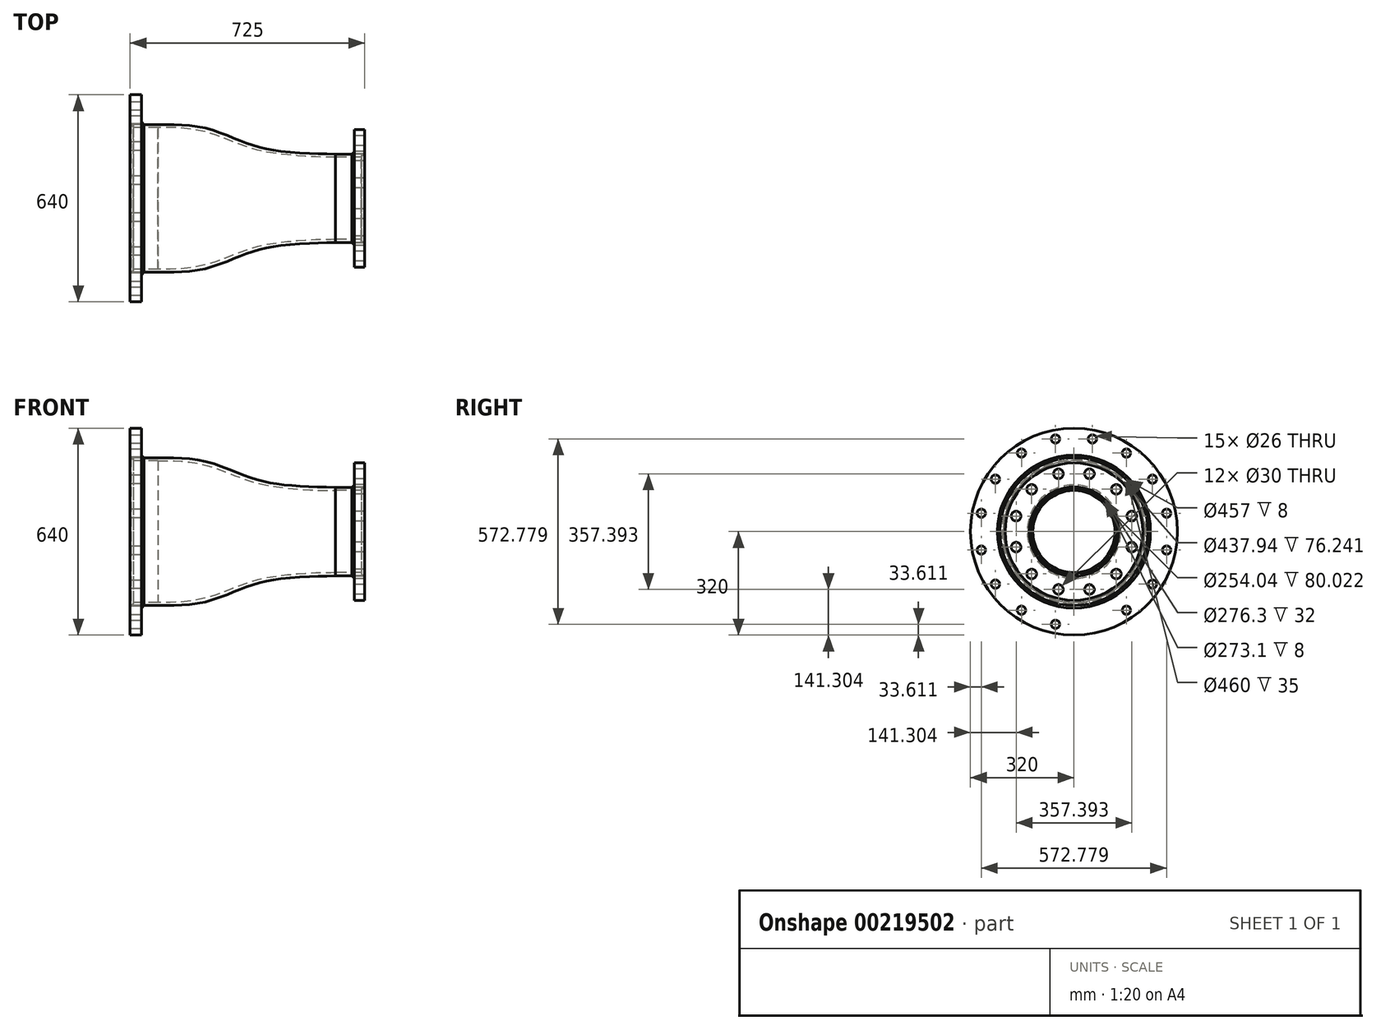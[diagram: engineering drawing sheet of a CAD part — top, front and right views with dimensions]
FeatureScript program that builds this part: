
annotation { "Feature Type Name" : "Feature", "Feature Type Description" : "" }
export const myFeature = defineFeature(function(context is Context, id is Id, definition is map)
    precondition{}
    {
        {
            var Q0;
            Q0=qCreatedBy(makeId("Front.planeOp"),FACE);
            var sketch = newSketch(context, id + "F0", { "sketchPlane" : qUnion([Q0])});
            skLineSegment(sketch, "E0", {"start": v(-562.58, 0) * mm, "end": v(652.64, 0) * mm, "construction": true});
            skLineSegment(sketch, "E1", {"start": v(-329.66, 228.5) * mm, "end": v(-253.37, 228.5) * mm});
            skLineSegment(sketch, "E2", {"start": v(375.34, 136.55) * mm, "end": v(295.32, 136.55) * mm});
            skFitSpline(sketch, "E3", {"points": [v(-253.37, 228.5) * mm, v(-109.72, 217.61) * mm, v(24.3, 169.13) * mm, v(129.85, 145.37) * mm, v(295.32, 136.55) * mm], "startDerivative": vector(539.24, -5.2) * mm, "endDerivative": vector(650.78, -14.67) * mm});
            skLineSegment(sketch, "E4.1", {"start": v(-329.66, 218.97) * mm, "end": v(-253.42, 218.97) * mm});
            skLineSegment(sketch, "E5.0", {"start": v(375.34, 127.02) * mm, "end": v(295.32, 127.02) * mm});
            skLineSegment(sketch, "E6", {"start": v(-329.66, 228.5) * mm, "end": v(-329.66, 218.97) * mm});
            skLineSegment(sketch, "E7", {"start": v(375.34, 136.55) * mm, "end": v(375.34, 127.02) * mm});
            skLineSegment(sketch, "E8.bottom", {"start": v(-304.66, 230) * mm, "end": v(-339.66, 230) * mm});
            skLineSegment(sketch, "E8.top", {"start": v(-304.66, 320) * mm, "end": v(-339.66, 320) * mm});
            skLineSegment(sketch, "E8.left", {"start": v(-304.66, 230) * mm, "end": v(-304.66, 320) * mm});
            skLineSegment(sketch, "E8.right", {"start": v(-339.66, 230) * mm, "end": v(-339.66, 320) * mm});
            skLineSegment(sketch, "E9", {"start": v(-304.66, 230) * mm, "end": v(-304.66, 228.5) * mm});
            skLineSegment(sketch, "E10", {"start": v(-337.66, 230) * mm, "end": v(-329.66, 222) * mm});
            skLineSegment(sketch, "E11", {"start": v(-304.66, 236.5) * mm, "end": v(-296.66, 228.5) * mm});
            skLineSegment(sketch, "E12", {"start": v(-329.66, 230) * mm, "end": v(-329.66, 228.5) * mm});
            skLineSegment(sketch, "E13.bottom", {"start": v(385.34, 138.15) * mm, "end": v(353.34, 138.15) * mm});
            skLineSegment(sketch, "E13.top", {"start": v(385.34, 212.5) * mm, "end": v(353.34, 212.5) * mm});
            skLineSegment(sketch, "E13.left", {"start": v(385.34, 138.15) * mm, "end": v(385.34, 212.5) * mm});
            skLineSegment(sketch, "E13.right", {"start": v(353.34, 138.15) * mm, "end": v(353.34, 212.5) * mm});
            skLineSegment(sketch, "E14", {"start": v(353.34, 138.15) * mm, "end": v(353.34, 136.55) * mm});
            skLineSegment(sketch, "E15", {"start": v(375.34, 138.15) * mm, "end": v(375.34, 136.55) * mm});
            skLineSegment(sketch, "E16", {"start": v(345.34, 136.55) * mm, "end": v(353.34, 144.55) * mm});
            skLineSegment(sketch, "E17", {"start": v(383.34, 138.15) * mm, "end": v(375.34, 130.15) * mm});
            skLineSegment(sketch, "E18", {"start": v(-253.37, 228.5) * mm, "end": v(-253.42, 218.97) * mm});
            skLineSegment(sketch, "E19", {"start": v(295.32, 136.55) * mm, "end": v(295.32, 127.02) * mm});
            skFitSpline(sketch, "E20", {"points": [v(-253.42, 218.97) * mm, v(-209.6, 218.97) * mm, v(-109.6, 206.39) * mm, v(24.68, 158.26) * mm, v(130.86, 136.31) * mm, v(236.57, 128.15) * mm, v(295.32, 127.02) * mm], "startDerivative": vector(341.33, 5.53) * mm, "endDerivative": vector(401.2, -2.2) * mm});
            skSolve(sketch);
        }
        {
            var Q0;
            {var subQ0=sQuery(id+"F0.wireOp",EDGE,"E8.top");Q0=makeQuery(id+"F0.imprint","IMPRINT",FACE,{"disambiguationData":[TD([[makeQuery(id+"F0.imprint","IMPRINT",EDGE,{"derivedFrom":subQ0}),1.0]])]});}
            var Q1;
            Q1=sQuery(id+"F0.wireOp",EDGE,"E0");
            revolve(context, id + "F1", {"entities" : qUnion([Q0]), "axis" : qUnion([Q1]), "revolveType" : RevolveType.FULL});
        }
        {
            var Q0;
            Q0=makeQuery(id+"F0.imprint","IMPRINT",FACE,{"disambiguationData":[TD([[makeQuery(id+"F0.imprint","IMPRINT",EDGE,{"derivedFrom":sQuery(id+"F0.wireOp",EDGE,"E3")}),-1.0]])]});
            var Q1;
            {var subQ0=sQuery(id+"F0.wireOp",EDGE,"E4.1");Q1=makeQuery(id+"F0.imprint","IMPRINT",FACE,{"disambiguationData":[TD([[makeQuery(id+"F0.imprint","IMPRINT",EDGE,{"derivedFrom":subQ0}),1.0]])]});}
            var Q2;
            {var subQ0=sQuery(id+"F0.wireOp",EDGE,"E5.0");Q2=makeQuery(id+"F0.imprint","IMPRINT",FACE,{"disambiguationData":[TD([[makeQuery(id+"F0.imprint","IMPRINT",EDGE,{"derivedFrom":subQ0}),-1.0]])]});}
            var Q3;
            Q3=sQuery(id+"F0.wireOp",EDGE,"E0");
            revolve(context, id + "F2", {"entities" : qUnion([Q0, Q1, Q2]), "axis" : qUnion([Q3]), "revolveType" : RevolveType.FULL});
        }
        {
            var Q0;
            {var subQ0=sQuery(id+"F0.wireOp",EDGE,"E13.top");Q0=makeQuery(id+"F0.imprint","IMPRINT",FACE,{"disambiguationData":[TD([[makeQuery(id+"F0.imprint","IMPRINT",EDGE,{"derivedFrom":subQ0}),1.0]])]});}
            var Q1;
            Q1=sQuery(id+"F0.wireOp",EDGE,"E0");
            revolve(context, id + "F3", {"entities" : qUnion([Q0]), "axis" : qUnion([Q1]), "revolveType" : RevolveType.FULL});
        }
        {
            var Q0;
            {var subQ2=sQuery(id+"F0.wireOp",EDGE,"E10");Q0=makeQuery(id+"F0.imprint","IMPRINT",FACE,{"disambiguationData":[TD([[makeQuery(id+"F0.imprint","IMPRINT",EDGE,{"derivedFrom":subQ2}),1.0]])]});}
            var Q1;
            {var subQ0=sQuery(id+"F0.wireOp",EDGE,"E9");Q1=makeQuery(id+"F0.imprint","IMPRINT",FACE,{"disambiguationData":[TD([[makeQuery(id+"F0.imprint","IMPRINT",EDGE,{"derivedFrom":subQ0}),1.0]])]});}
            var Q2;
            {var subQ0=sQuery(id+"F0.wireOp",EDGE,"E14");Q2=makeQuery(id+"F0.imprint","IMPRINT",FACE,{"disambiguationData":[TD([[makeQuery(id+"F0.imprint","IMPRINT",EDGE,{"derivedFrom":subQ0}),-1.0]])]});}
            var Q3;
            {var subQ0=sQuery(id+"F0.wireOp",EDGE,"E15");Q3=makeQuery(id+"F0.imprint","IMPRINT",FACE,{"disambiguationData":[TD([[makeQuery(id+"F0.imprint","IMPRINT",EDGE,{"derivedFrom":subQ0}),1.0]])]});}
            var Q4;
            Q4=sQuery(id+"F0.wireOp",EDGE,"E0");
            revolve(context, id + "F4", {"entities" : qUnion([Q0, Q1, Q2, Q3]), "axis" : qUnion([Q4]), "revolveType" : RevolveType.FULL});
        }
        {
            var Q0;
            Q0=makeQuery(id+"F3.opRevolve","SWEPT_FACE",FACE,{"disambiguationData":[OSD([sQuery(id+"F0.wireOp",EDGE,"E13.left")])]});
            var sketch = newSketch(context, id + "F5", { "sketchPlane" : qUnion([Q0])});
            skCircle(sketch, "E21.cCircle", {"center": v(0, 0) * mm, "radius": 185 * mm, "construction": true});
            skLineSegment(sketch, "E21.0", {"start": v(130.81, 130.81) * mm, "end": v(178.7, 47.88) * mm});
            skLineSegment(sketch, "E21.1", {"start": v(178.7, 47.88) * mm, "end": v(178.7, -47.88) * mm});
            skLineSegment(sketch, "E21.2", {"start": v(178.7, -47.88) * mm, "end": v(130.81, -130.81) * mm});
            skLineSegment(sketch, "E21.3", {"start": v(130.81, -130.81) * mm, "end": v(47.88, -178.7) * mm});
            skLineSegment(sketch, "E21.4", {"start": v(47.88, -178.7) * mm, "end": v(-47.88, -178.7) * mm});
            skLineSegment(sketch, "E21.5", {"start": v(-47.88, -178.7) * mm, "end": v(-130.81, -130.81) * mm});
            skLineSegment(sketch, "E21.6", {"start": v(-130.81, -130.81) * mm, "end": v(-178.7, -47.88) * mm});
            skLineSegment(sketch, "E21.7", {"start": v(-178.7, -47.88) * mm, "end": v(-178.7, 47.88) * mm});
            skLineSegment(sketch, "E21.8", {"start": v(-178.7, 47.88) * mm, "end": v(-130.81, 130.81) * mm});
            skLineSegment(sketch, "E21.9", {"start": v(-130.81, 130.81) * mm, "end": v(-47.88, 178.7) * mm});
            skLineSegment(sketch, "E21.10", {"start": v(-47.88, 178.7) * mm, "end": v(47.88, 178.7) * mm});
            skLineSegment(sketch, "E21.11", {"start": v(47.88, 178.7) * mm, "end": v(130.81, 130.81) * mm});
            skPoint(sketch, "E22", {"position": v(130.81, 130.81) * mm});
            skPoint(sketch, "E23", {"position": v(178.7, 47.88) * mm});
            skPoint(sketch, "E24", {"position": v(178.7, -47.88) * mm});
            skPoint(sketch, "E25", {"position": v(130.81, -130.81) * mm});
            skPoint(sketch, "E26", {"position": v(47.88, -178.7) * mm});
            skPoint(sketch, "E27", {"position": v(-47.88, -178.7) * mm});
            skPoint(sketch, "E28", {"position": v(-130.81, -130.81) * mm});
            skPoint(sketch, "E29", {"position": v(-178.7, -47.88) * mm});
            skPoint(sketch, "E30", {"position": v(-178.7, 47.88) * mm});
            skPoint(sketch, "E31", {"position": v(-130.81, 130.81) * mm});
            skPoint(sketch, "E32", {"position": v(-47.88, 178.7) * mm});
            skPoint(sketch, "E33", {"position": v(47.88, 178.7) * mm});
            skSolve(sketch);
        }
        {
            var Q0;
            Q0=sQuery(id+"F5.wireOp",VERTEX,"E23");
            var Q1;
            Q1=sQuery(id+"F5.wireOp",VERTEX,"E24");
            var Q2;
            Q2=sQuery(id+"F5.wireOp",VERTEX,"E25");
            var Q3;
            Q3=sQuery(id+"F5.wireOp",VERTEX,"E26");
            var Q4;
            Q4=sQuery(id+"F5.wireOp",VERTEX,"E27");
            var Q5;
            Q5=sQuery(id+"F5.wireOp",VERTEX,"E28");
            var Q6;
            Q6=sQuery(id+"F5.wireOp",VERTEX,"E29");
            var Q7;
            Q7=sQuery(id+"F5.wireOp",VERTEX,"E30");
            var Q8;
            Q8=sQuery(id+"F5.wireOp",VERTEX,"E31");
            var Q9;
            Q9=sQuery(id+"F5.wireOp",VERTEX,"E32");
            var Q10;
            Q10=sQuery(id+"F5.wireOp",VERTEX,"E33");
            var Q11;
            Q11=sQuery(id+"F5.wireOp",VERTEX,"E22");
            var Q12;
            Q12=makeQuery(id+"F3.opRevolve","SWEPT_BODY",BODY,{"disambiguationData":[OSD([sQuery(id+"F0.wireOp",EDGE,"E13.bottom"),sQuery(id+"F0.wireOp",EDGE,"E13.top"),sQuery(id+"F0.wireOp",EDGE,"E13.left"),sQuery(id+"F0.wireOp",EDGE,"E13.right")])]});
            hole(context, id + "F6", {"style" : HoleStyle.SIMPLE, "endStyle" : HoleEndStyle.BLIND, "holeDiameter" : 30 * mm, "holeDepth" : 50 * mm, "locations" : qUnion([Q0, Q1, Q2, Q3, Q4, Q5, Q6, Q7, Q8, Q9, Q10, Q11]), "scope" : qUnion([Q12])});
        }
        {
            var Q0;
            Q0=makeQuery(id+"F1.opRevolve","SWEPT_FACE",FACE,{"disambiguationData":[OSD([sQuery(id+"F0.wireOp",EDGE,"E8.right")])]});
            var sketch = newSketch(context, id + "F7", { "sketchPlane" : qUnion([Q0])});
            skCircle(sketch, "E34.cCircle", {"center": v(0, 0) * mm, "radius": 292 * mm, "construction": true});
            skLineSegment(sketch, "E34.0", {"start": v(56.97, 286.39) * mm, "end": v(162.23, 242.79) * mm});
            skLineSegment(sketch, "E34.1", {"start": v(162.23, 242.79) * mm, "end": v(242.79, 162.23) * mm});
            skLineSegment(sketch, "E34.2", {"start": v(242.79, 162.23) * mm, "end": v(286.39, 56.97) * mm});
            skLineSegment(sketch, "E34.3", {"start": v(286.39, 56.97) * mm, "end": v(286.39, -56.97) * mm});
            skLineSegment(sketch, "E34.4", {"start": v(286.39, -56.97) * mm, "end": v(242.79, -162.23) * mm});
            skLineSegment(sketch, "E34.5", {"start": v(242.79, -162.23) * mm, "end": v(162.23, -242.79) * mm});
            skLineSegment(sketch, "E34.6", {"start": v(162.23, -242.79) * mm, "end": v(56.97, -286.39) * mm});
            skLineSegment(sketch, "E34.7", {"start": v(56.97, -286.39) * mm, "end": v(-56.97, -286.39) * mm});
            skLineSegment(sketch, "E34.8", {"start": v(-56.97, -286.39) * mm, "end": v(-162.23, -242.79) * mm});
            skLineSegment(sketch, "E34.9", {"start": v(-162.23, -242.79) * mm, "end": v(-242.79, -162.23) * mm});
            skLineSegment(sketch, "E34.10", {"start": v(-242.79, -162.23) * mm, "end": v(-286.39, -56.97) * mm});
            skLineSegment(sketch, "E34.11", {"start": v(-286.39, -56.97) * mm, "end": v(-286.39, 56.97) * mm});
            skLineSegment(sketch, "E34.12", {"start": v(-286.39, 56.97) * mm, "end": v(-242.79, 162.23) * mm});
            skLineSegment(sketch, "E34.13", {"start": v(-242.79, 162.23) * mm, "end": v(-162.23, 242.79) * mm});
            skLineSegment(sketch, "E34.14", {"start": v(-162.23, 242.79) * mm, "end": v(-56.97, 286.39) * mm});
            skLineSegment(sketch, "E34.15", {"start": v(-56.97, 286.39) * mm, "end": v(56.97, 286.39) * mm});
            skPoint(sketch, "E35", {"position": v(-56.97, 286.39) * mm});
            skPoint(sketch, "E36", {"position": v(56.97, 286.39) * mm});
            skPoint(sketch, "E37", {"position": v(162.23, 242.79) * mm});
            skPoint(sketch, "E38", {"position": v(242.79, 162.23) * mm});
            skPoint(sketch, "E39", {"position": v(286.39, 56.97) * mm});
            skPoint(sketch, "E40", {"position": v(286.39, -56.97) * mm});
            skPoint(sketch, "E41", {"position": v(242.79, -162.23) * mm});
            skPoint(sketch, "E42", {"position": v(162.23, -242.79) * mm});
            skPoint(sketch, "E43", {"position": v(56.97, -286.39) * mm});
            skPoint(sketch, "E44", {"position": v(-56.97, -286.39) * mm});
            skPoint(sketch, "E45", {"position": v(-162.23, -242.79) * mm});
            skPoint(sketch, "E46", {"position": v(-242.79, -162.23) * mm});
            skPoint(sketch, "E47", {"position": v(-286.39, -56.97) * mm});
            skPoint(sketch, "E48", {"position": v(-286.39, 56.97) * mm});
            skPoint(sketch, "E49", {"position": v(-242.79, 162.23) * mm});
            skPoint(sketch, "E50", {"position": v(-162.23, 242.79) * mm});
            skSolve(sketch);
        }
        {
            var Q0;
            Q0=sQuery(id+"F7.wireOp",VERTEX,"E50");
            var Q1;
            Q1=sQuery(id+"F7.wireOp",VERTEX,"E49");
            var Q2;
            Q2=sQuery(id+"F7.wireOp",VERTEX,"E48");
            var Q3;
            Q3=sQuery(id+"F7.wireOp",VERTEX,"E47");
            var Q4;
            Q4=sQuery(id+"F7.wireOp",VERTEX,"E46");
            var Q5;
            Q5=sQuery(id+"F7.wireOp",VERTEX,"E35");
            var Q6;
            Q6=sQuery(id+"F7.wireOp",VERTEX,"E36");
            var Q7;
            Q7=sQuery(id+"F7.wireOp",VERTEX,"E37");
            var Q8;
            Q8=sQuery(id+"F7.wireOp",VERTEX,"E38");
            var Q9;
            Q9=sQuery(id+"F7.wireOp",VERTEX,"E39");
            var Q10;
            Q10=sQuery(id+"F7.wireOp",VERTEX,"E40");
            var Q11;
            Q11=sQuery(id+"F7.wireOp",VERTEX,"E41");
            var Q12;
            Q12=sQuery(id+"F7.wireOp",VERTEX,"E42");
            var Q13;
            Q13=sQuery(id+"F7.wireOp",VERTEX,"E43");
            var Q14;
            Q14=sQuery(id+"F7.wireOp",VERTEX,"E45");
            var Q15;
            Q15=makeQuery(id+"F1.opRevolve","SWEPT_BODY",BODY,{"disambiguationData":[OSD([sQuery(id+"F0.wireOp",EDGE,"E8.bottom"),sQuery(id+"F0.wireOp",EDGE,"E8.top"),sQuery(id+"F0.wireOp",EDGE,"E8.left"),sQuery(id+"F0.wireOp",EDGE,"E8.right")])]});
            hole(context, id + "F8", {"style" : HoleStyle.SIMPLE, "endStyle" : HoleEndStyle.THROUGH, "holeDiameter" : 26 * mm, "majorDiameter" : 5 * mm, "isTappedThrough" : true, "tappedDepth" : 15.2 * mm, "tapClearance" : 3, "startFromSketch" : true, "locations" : qUnion([Q0, Q1, Q2, Q3, Q4, Q5, Q6, Q7, Q8, Q9, Q10, Q11, Q12, Q13, Q14]), "scope" : qUnion([Q15])});
        }
    });
